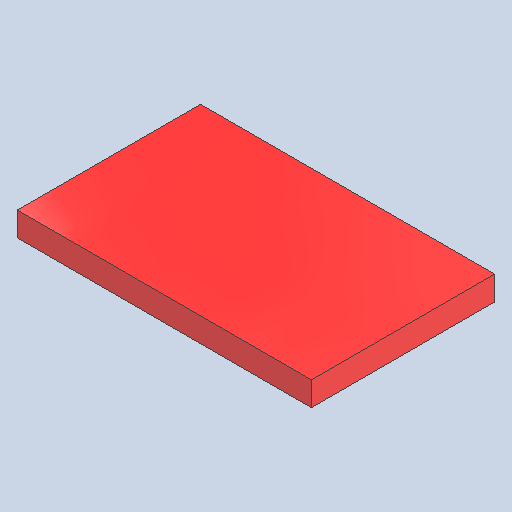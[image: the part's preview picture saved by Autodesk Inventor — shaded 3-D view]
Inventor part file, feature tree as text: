
AUTODESK INVENTOR PART (.ipt)
format: ipt  version: 2025.2 (Build 292293000, 293)  size: 94,720 bytes
history: native  units: mm
features: extrude x1, sketch x1
ambient origin geometry x8: Origin, YZ Plane, XZ Plane, XY Plane, X Axis, Y Axis, Z Axis, Center Point
bodies: Solid1 (feature_tree)
feature tree (2):
  extrude  "Extrusion1"  Depth=38.0mm
  sketch  "Sketch1"  dims[d0=61.0mm d1=38.0mm d2=5.0mm d3=0.0mm]
